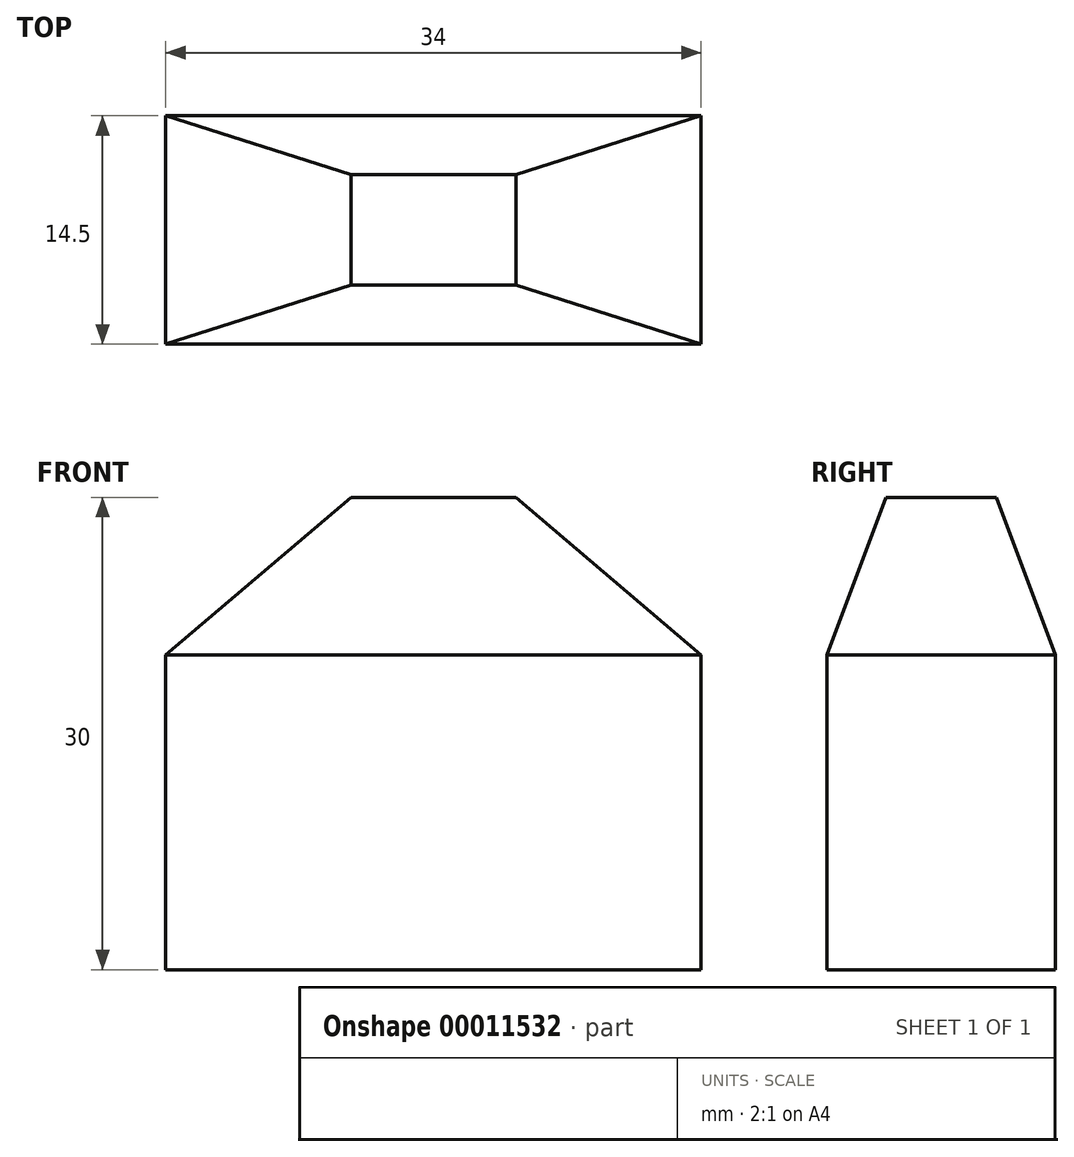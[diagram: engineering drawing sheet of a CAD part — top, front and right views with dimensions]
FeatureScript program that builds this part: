
annotation { "Feature Type Name" : "Feature", "Feature Type Description" : "" }
export const myFeature = defineFeature(function(context is Context, id is Id, definition is map)
    precondition{}
    {
        {
            var Q0;
            Q0=qCreatedBy(makeId("Top.planeOp"),FACE);
            var sketch = newSketch(context, id + "F0", { "sketchPlane" : qUnion([Q0])});
            skLineSegment(sketch, "E0.rect.bottom", {"start": v(17, -7.25) * mm, "end": v(-17, -7.25) * mm});
            skLineSegment(sketch, "E0.rect.top", {"start": v(17, 7.25) * mm, "end": v(-17, 7.25) * mm});
            skLineSegment(sketch, "E0.rect.left", {"start": v(17, -7.25) * mm, "end": v(17, 7.25) * mm});
            skLineSegment(sketch, "E0.rect.right", {"start": v(-17, -7.25) * mm, "end": v(-17, 7.25) * mm});
            skPoint(sketch, "E0.rect.middle", {"position": v(0, 0) * mm});
            skSolve(sketch);
        }
        {
            var Q0;
            Q0=makeQuery(id+"F0.imprint","IMPRINT",FACE,{"disambiguationData":[TD([[makeQuery(id+"F0.imprint","IMPRINT",EDGE,{"derivedFrom":sQuery(id+"F0.wireOp",EDGE,"E0.rect.bottom")}),-1.0]])]});
            extrude(context, id + "F1", {"entities" : qUnion([Q0]), "depth" : 20 * mm});
        }
        {
            var Q0;
            Q0=makeQuery(id+"F1.opExtrude","SWEPT_FACE",FACE,{"disambiguationData":[OSD([sQuery(id+"F0.wireOp",EDGE,"E0.rect.bottom")])]});
            var sketch = newSketch(context, id + "F2", { "sketchPlane" : qUnion([Q0])});
            skLineSegment(sketch, "E1", {"start": v(-17, 20) * mm, "end": v(-5.24, 30) * mm});
            skLineSegment(sketch, "E2", {"start": v(-5.24, 30) * mm, "end": v(5.24, 30) * mm});
            skLineSegment(sketch, "E3", {"start": v(5.24, 30) * mm, "end": v(17, 20) * mm});
            skSolve(sketch);
        }
        {
            var Q0;
            Q0=makeQuery(id+"F2.imprint","IMPRINT",FACE,{"disambiguationData":[TD([[makeQuery(id+"F2.imprint","IMPRINT",EDGE,{"derivedFrom":sQuery(id+"F2.wireOp",EDGE,"E1")}),-1.0]])]});
            var Q1;
            Q1=makeQuery(id+"F1.opExtrude","SWEPT_FACE",FACE,{"disambiguationData":[OSD([sQuery(id+"F0.wireOp",EDGE,"E0.rect.top")])]});
            extrude(context, id + "F3", {"entities" : qUnion([Q0]), "operationType" : NewBodyOperationType.ADD, "endBound" : BoundingType.UP_TO_SURFACE, "oppositeDirection" : true, "endBoundEntityFace" : qUnion([Q1]), "depth" : 25 * mm});
        }
        {
            var Q0;
            Q0=makeQuery(id+"F1.opExtrude","SWEPT_FACE",FACE,{"disambiguationData":[OSD([sQuery(id+"F0.wireOp",EDGE,"E0.rect.right")])]});
            var sketch = newSketch(context, id + "F4", { "sketchPlane" : qUnion([Q0])});
            skLineSegment(sketch, "E4.0.0", {"start": v(7.25, 30) * mm, "end": v(-7.25, 30) * mm});
            skLineSegment(sketch, "E4.0.1", {"start": v(-7.25, 30) * mm, "end": v(-7.25, 20) * mm});
            skLineSegment(sketch, "E4.0.2", {"start": v(-7.25, 20) * mm, "end": v(7.25, 20) * mm});
            skLineSegment(sketch, "E4.0.3", {"start": v(7.25, 20) * mm, "end": v(7.25, 30) * mm});
            skLineSegment(sketch, "E5", {"start": v(-7.25, 20) * mm, "end": v(-3.5, 30) * mm});
            skLineSegment(sketch, "E6", {"start": v(7.25, 20) * mm, "end": v(3.5, 30) * mm});
            skSolve(sketch);
        }
        {
            var Q0;
            {var subQ0=sQuery(id+"F4.wireOp",EDGE,"E4.0.1");Q0=makeQuery(id+"F4.imprint","IMPRINT",FACE,{"disambiguationData":[TD([[makeQuery(id+"F4.imprint","IMPRINT",EDGE,{"derivedFrom":subQ0}),1.0]])]});}
            var Q1;
            {var subQ1=sQuery(id+"F4.wireOp",EDGE,"E4.0.3");Q1=makeQuery(id+"F4.imprint","IMPRINT",FACE,{"disambiguationData":[TD([[makeQuery(id+"F4.imprint","IMPRINT",EDGE,{"derivedFrom":subQ1}),1.0]])]});}
            extrude(context, id + "F5", {"entities" : qUnion([Q0, Q1]), "operationType" : NewBodyOperationType.REMOVE, "endBound" : BoundingType.THROUGH_ALL, "oppositeDirection" : true, "depth" : 25 * mm});
        }
    });
